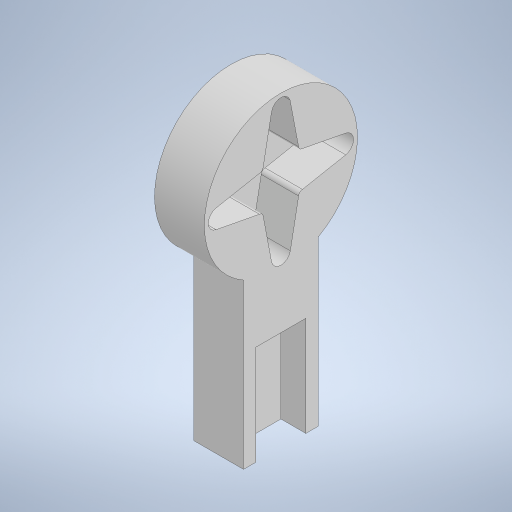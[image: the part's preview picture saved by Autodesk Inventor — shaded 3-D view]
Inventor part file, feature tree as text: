
AUTODESK INVENTOR PART (.ipt)
format: ipt  version: 2023 (Build 270158000, 158)  size: 302,080 bytes
history: native  units: in
note: dims shown in document units (in); Inventor stores cm internally (conversion verified against a paired STEP export)
features: extrude x5, sketch x4, projected_geometry x3
ambient origin geometry x8: Origin, YZ Plane, XZ Plane, XY Plane, X Axis, Y Axis, Z Axis, Center Point
bodies: Solid1 (feature_tree)
feature tree (12):
  extrude  "Extrusion1"  Depth=0.75in
  extrude  "Extrusion3"  Depth=0.5in
  extrude  "Extrusion4"  Depth=1.0in
  sketch  "Sketch5"  dims[d21=0.25in d22=0.0in d25=0.625in d26=0.0625in d27=0.0in d28=0.75in d29=0.0in d30=0.02in d31=1.0in d32=0.0in d33=0.375in d34=0.0in]
  extrude  "Extrusion5"  Depth=0.625in TaperAngle=0.0deg
  extrude  "Extrusion6"  Depth=0.75in
  sketch  "Sketch1"  dims[d0=0.75in d1=2.5in]
  sketch  "Sketch3"  dims[d2=0.5in d3=0.0in d18=0.5in]
  projected_geometry  "Projected Loop2"
  sketch  "Sketch4"  dims[d19=0.25in d20=1.0in]
  projected_geometry  "Projected Loop3"
  projected_geometry  "Projected Loop4"
